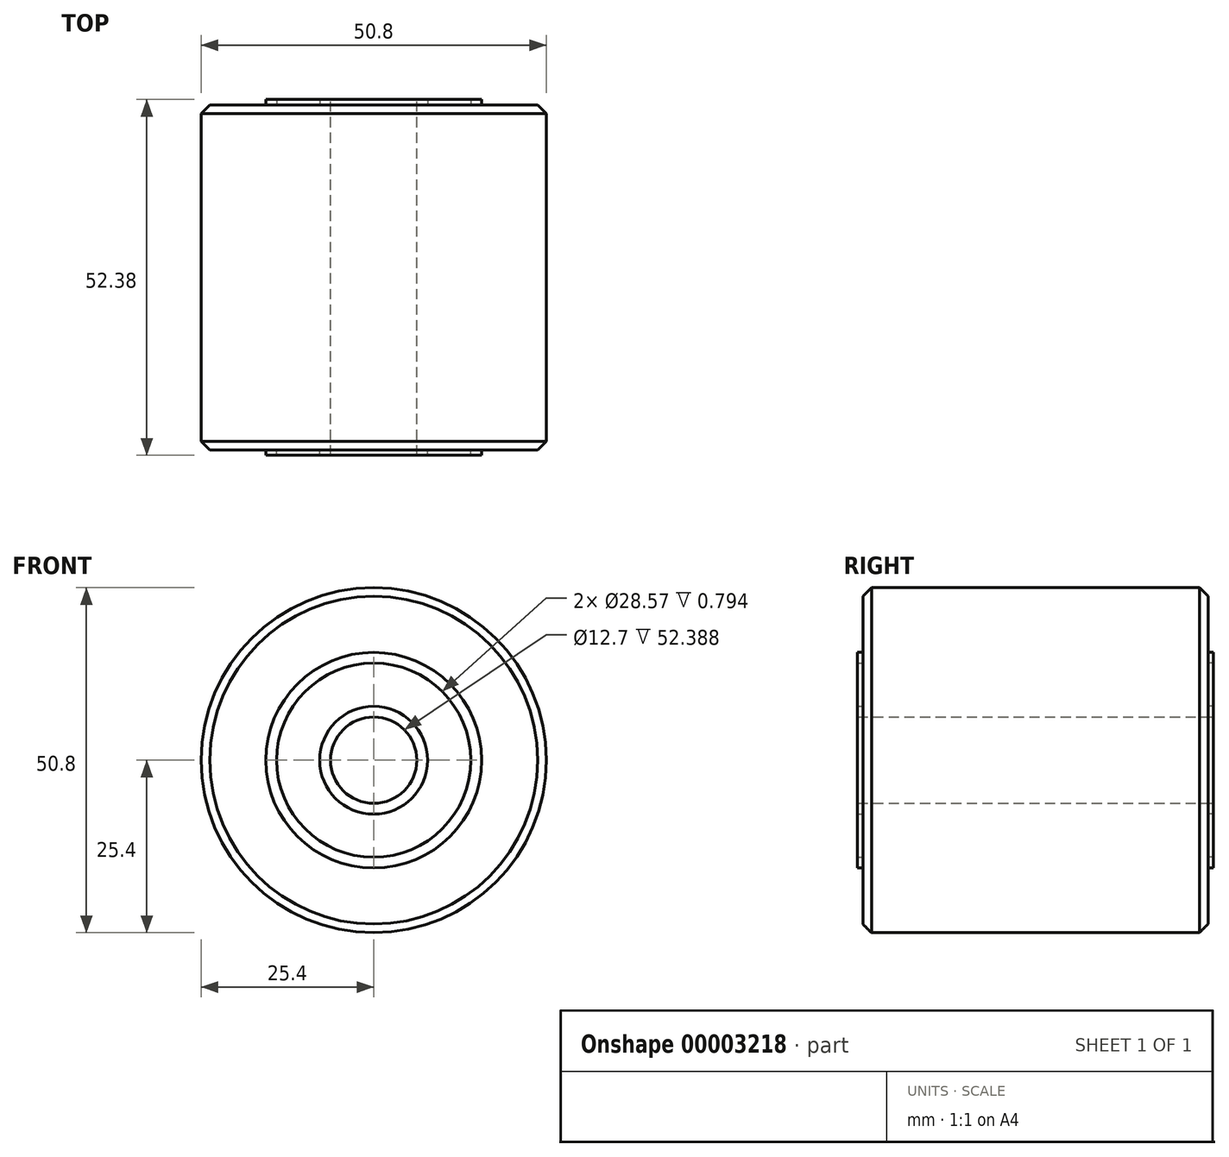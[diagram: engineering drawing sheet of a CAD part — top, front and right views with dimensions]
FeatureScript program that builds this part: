
annotation { "Feature Type Name" : "Feature", "Feature Type Description" : "" }
export const myFeature = defineFeature(function(context is Context, id is Id, definition is map)
    precondition{}
    {
        {
            var Q0;
            Q0=qCreatedBy(makeId("Front.planeOp"),FACE);
            var sketch = newSketch(context, id + "F0", { "sketchPlane" : qUnion([Q0])});
            skCircle(sketch, "E0", {"center": v(0, 0) * mm, "radius": 25.4 * mm});
            skCircle(sketch, "E1", {"center": v(0, 0) * mm, "radius": 6.35 * mm});
            skSolve(sketch);
        }
        {
            var Q0;
            Q0 = qSketchRegion(id + "F0", true);
            extrude(context, id + "F1", {"entities" : qUnion([Q0]), "endBound" : BoundingType.SYMMETRIC, "depth" : 50.8 * mm});
        }
        {
            var Q0;
            Q0=makeQuery(id+"F1.opExtrude","CAP_EDGE",EDGE,{"disambiguationData":[OSD([sQuery(id+"F0.wireOp",EDGE,"E0")])],"isStart":false});
            var Q1;
            Q1=makeQuery(id+"F1.opExtrude","CAP_EDGE",EDGE,{"disambiguationData":[OSD([sQuery(id+"F0.wireOp",EDGE,"E0")])],"isStart":true});
            chamfer(context, id + "F2", {"entities" : qUnion([Q0, Q1]), "width" : 1.27 * mm, "tangentPropagation" : true});
        }
        {
            var Q0;
            Q0=makeQuery(id+"F1.opExtrude","CAP_FACE",FACE,{"disambiguationData":[OSD([sQuery(id+"F0.wireOp",EDGE,"E0"),sQuery(id+"F0.wireOp",EDGE,"E1")])],"isStart":false});
            var sketch = newSketch(context, id + "F3", { "sketchPlane" : qUnion([Q0])});
            skCircle(sketch, "E2", {"center": v(0, 0) * mm, "radius": 7.94 * mm});
            skCircle(sketch, "E3", {"center": v(0, 0) * mm, "radius": 14.29 * mm});
            skCircle(sketch, "E4", {"center": v(0, 0) * mm, "radius": 25.13 * mm});
            skCircle(sketch, "E5", {"center": v(0, 0) * mm, "radius": 15.88 * mm});
            skSolve(sketch);
        }
        {
            var Q0;
            Q0=makeQuery(id+"F3.imprint","IMPRINT",FACE,{"disambiguationData":[TD([[makeQuery(id+"F3.imprint","IMPRINT",EDGE,{"derivedFrom":sQuery(id+"F3.wireOp",EDGE,"E2")}),1.0]])]});
            var Q1;
            Q1=makeQuery(id+"F3.imprint","IMPRINT",FACE,{"disambiguationData":[TD([[makeQuery(id+"F3.imprint","IMPRINT",EDGE,{"derivedFrom":sQuery(id+"F3.wireOp",EDGE,"E3")}),-1.0]])]});
            extrude(context, id + "F4", {"entities" : qUnion([Q0, Q1]), "operationType" : NewBodyOperationType.ADD, "depth" : 0.8 * mm});
        }
        {
            var Q0;
            Q0=makeQuery(id+"F1.opExtrude","CAP_FACE",FACE,{"disambiguationData":[OSD([sQuery(id+"F0.wireOp",EDGE,"E0"),sQuery(id+"F0.wireOp",EDGE,"E1")])],"isStart":true});
            var sketch = newSketch(context, id + "F5", { "sketchPlane" : qUnion([Q0])});
            skCircle(sketch, "E6", {"center": v(0, 0) * mm, "radius": 7.94 * mm});
            skCircle(sketch, "E7", {"center": v(0, 0) * mm, "radius": 14.29 * mm});
            skCircle(sketch, "E8", {"center": v(0, 0) * mm, "radius": 15.88 * mm});
            skSolve(sketch);
        }
        {
            var Q0;
            Q0=makeQuery(id+"F5.imprint","IMPRINT",FACE,{"disambiguationData":[TD([[makeQuery(id+"F5.imprint","IMPRINT",EDGE,{"derivedFrom":sQuery(id+"F5.wireOp",EDGE,"E6")}),1.0]])]});
            var Q1;
            Q1=makeQuery(id+"F5.imprint","IMPRINT",FACE,{"disambiguationData":[TD([[makeQuery(id+"F5.imprint","IMPRINT",EDGE,{"derivedFrom":sQuery(id+"F5.wireOp",EDGE,"E7")}),-1.0]])]});
            extrude(context, id + "F6", {"entities" : qUnion([Q0, Q1]), "operationType" : NewBodyOperationType.ADD, "depth" : 0.8 * mm});
        }
    });
